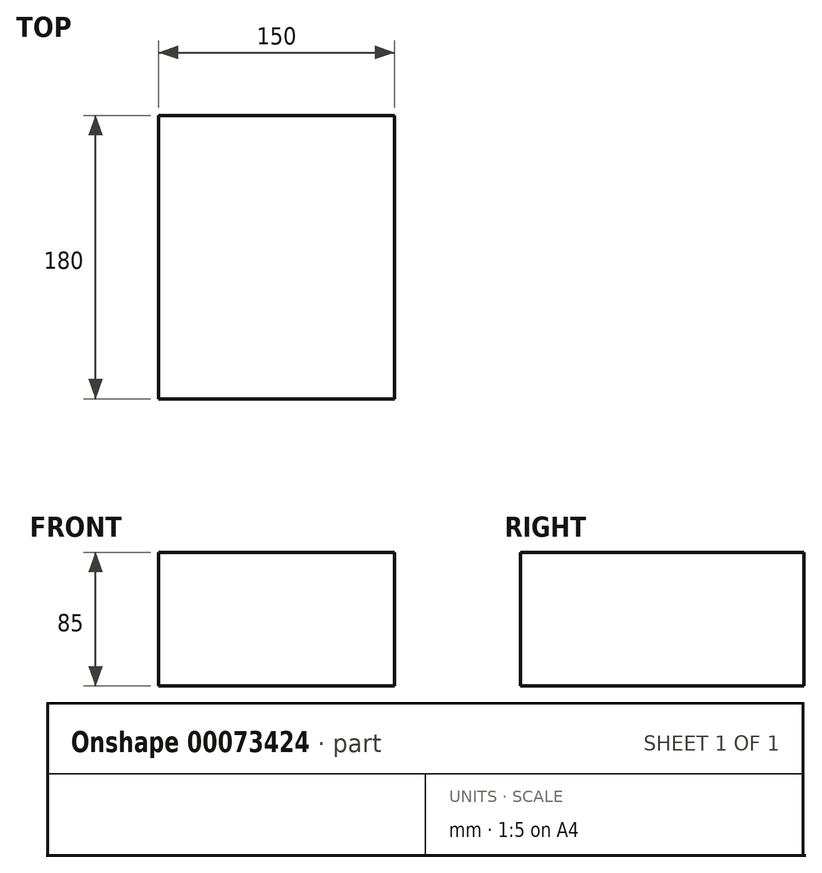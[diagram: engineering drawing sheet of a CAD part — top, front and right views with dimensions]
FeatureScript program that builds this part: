
annotation { "Feature Type Name" : "Feature", "Feature Type Description" : "" }
export const myFeature = defineFeature(function(context is Context, id is Id, definition is map)
    precondition{}
    {
        {
            var Q0;
            Q0=qCreatedBy(makeId("Front.planeOp"),FACE);
            var sketch = newSketch(context, id + "F0", { "sketchPlane" : qUnion([Q0])});
            skCircle(sketch, "E0", {"center": v(0, 0) * mm, "radius": 30 * mm});
            skSolve(sketch);
        }
        {
            var Q0;
            Q0 = qSketchRegion(id + "F0", true);
            extrude(context, id + "F1", {"entities" : qUnion([Q0]), "depth" : 190 * mm});
        }
        {
            var Q0;
            Q0=makeQuery(id+"F1.opExtrude","CAP_FACE",FACE,{"disambiguationData":[OSD([sQuery(id+"F0.wireOp",EDGE,"E0")])],"isStart":true});
            var sketch = newSketch(context, id + "F2", { "sketchPlane" : qUnion([Q0])});
            skArc(sketch, "E1", {"start": v(0, 40) * mm, "mid": v(-40, 0) * mm, "end": v(0, -40) * mm});
            skLineSegment(sketch, "E2", {"start": v(0, 40) * mm, "end": v(50, 40) * mm});
            skLineSegment(sketch, "E3", {"start": v(50, 40) * mm, "end": v(50, -40) * mm});
            skLineSegment(sketch, "E4", {"start": v(50, -40) * mm, "end": v(0, -40) * mm});
            skSolve(sketch);
        }
        {
            var Q0;
            Q0 = qSketchRegion(id + "F2", true);
            extrude(context, id + "F3", {"entities" : qUnion([Q0]), "operationType" : NewBodyOperationType.ADD, "oppositeDirection" : true, "depth" : 25 * mm});
        }
        {
            var Q0;
            Q0=makeQuery(id+"F3.opExtrude","CAP_FACE",FACE,{"disambiguationData":[OSD([sQuery(id+"F2.wireOp",EDGE,"E1"),sQuery(id+"F2.wireOp",EDGE,"E2"),sQuery(id+"F2.wireOp",EDGE,"E3"),sQuery(id+"F2.wireOp",EDGE,"E4")])],"isStart":false});
            var sketch = newSketch(context, id + "F4", { "sketchPlane" : qUnion([Q0])});
            skCircle(sketch, "E5", {"center": v(0, 0) * mm, "radius": 40 * mm});
            skSolve(sketch);
        }
        {
            var Q0;
            Q0 = qSketchRegion(id + "F4", true);
            extrude(context, id + "F5", {"entities" : qUnion([Q0]), "operationType" : NewBodyOperationType.ADD, "depth" : 35 * mm});
        }
        {
            var Q0;
            Q0=qCreatedBy(makeId("Front.planeOp"),FACE);
            var sketch = newSketch(context, id + "F6", { "sketchPlane" : qUnion([Q0])});
            skLineSegment(sketch, "E6.bottom", {"start": v(0, 0) * mm, "end": v(170, 0) * mm});
            skLineSegment(sketch, "E6.top", {"start": v(0, 170) * mm, "end": v(170, 170) * mm});
            skLineSegment(sketch, "E6.left", {"start": v(0, 0) * mm, "end": v(0, 170) * mm});
            skLineSegment(sketch, "E6.right", {"start": v(170, 0) * mm, "end": v(170, 170) * mm});
            skCircle(sketch, "E7", {"center": v(6.35, 159.84) * mm, "radius": 2 * mm});
            skCircle(sketch, "E8", {"center": v(163.83, 136.98) * mm, "radius": 2 * mm});
            skCircle(sketch, "E9", {"center": v(163.83, 4.9) * mm, "radius": 2 * mm});
            skCircle(sketch, "E10", {"center": v(6.35, 4.9) * mm, "radius": 2 * mm});
            skSolve(sketch);
        }
        {
            var Q0;
            Q0 = qSketchRegion(id + "F6", true);
            extrude(context, id + "F7", {"entities" : qUnion([Q0]), "depth" : 2 * mm});
        }
        {
            var Q0;
            Q0=makeQuery(id+"F7.opExtrude","SWEPT_BODY",BODY,{"disambiguationData":[OSD([sQuery(id+"F6.wireOp",EDGE,"E6.bottom"),sQuery(id+"F6.wireOp",EDGE,"E6.top"),sQuery(id+"F6.wireOp",EDGE,"E6.left"),sQuery(id+"F6.wireOp",EDGE,"E6.right"),sQuery(id+"F6.wireOp",EDGE,"E7"),sQuery(id+"F6.wireOp",EDGE,"E8"),sQuery(id+"F6.wireOp",EDGE,"E9"),sQuery(id+"F6.wireOp",EDGE,"E10")])]});
            deleteBodies(context, id + "F8", {"entities" : qUnion([Q0])});
        }
        {
            var Q0;
            Q0=qCreatedBy(makeId("Front.planeOp"),FACE);
            var sketch = newSketch(context, id + "F9", { "sketchPlane" : qUnion([Q0])});
            skLineSegment(sketch, "E11.bottom", {"start": v(0, 0) * mm, "end": v(150, 0) * mm});
            skLineSegment(sketch, "E11.top", {"start": v(0, 85) * mm, "end": v(150, 85) * mm});
            skLineSegment(sketch, "E11.left", {"start": v(0, 0) * mm, "end": v(0, 85) * mm});
            skLineSegment(sketch, "E11.right", {"start": v(150, 0) * mm, "end": v(150, 85) * mm});
            skSolve(sketch);
        }
        {
            var Q0;
            Q0 = qSketchRegion(id + "F9", true);
            extrude(context, id + "F10", {"entities" : qUnion([Q0]), "depth" : 180 * mm});
        }
        {
            var Q0;
            Q0=makeQuery(id+"F1.opExtrude","SWEPT_BODY",BODY,{"disambiguationData":[OSD([sQuery(id+"F0.wireOp",EDGE,"E0")])]});
            deleteBodies(context, id + "F11", {"entities" : qUnion([Q0])});
        }
    });
